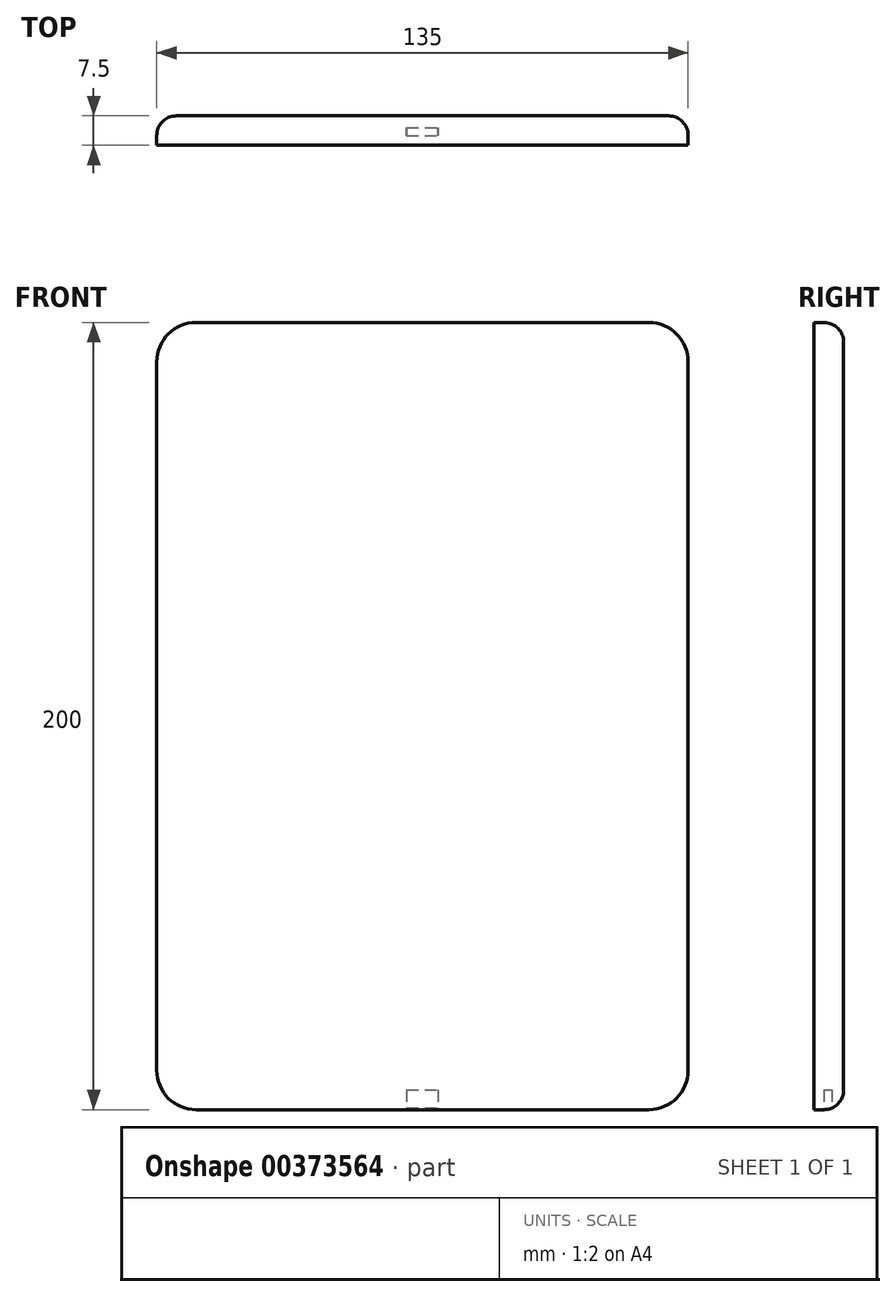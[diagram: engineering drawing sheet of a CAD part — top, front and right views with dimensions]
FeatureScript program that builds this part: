
annotation { "Feature Type Name" : "Feature", "Feature Type Description" : "" }
export const myFeature = defineFeature(function(context is Context, id is Id, definition is map)
    precondition{}
    {
        {
            var Q0;
            Q0=qCreatedBy(makeId("Front.planeOp"),FACE);
            var sketch = newSketch(context, id + "F0", { "sketchPlane" : qUnion([Q0])});
            skLineSegment(sketch, "E0.bottom", {"start": v(0, 0) * mm, "end": v(135, 0) * mm});
            skLineSegment(sketch, "E0.top", {"start": v(0, 200) * mm, "end": v(135, 200) * mm});
            skLineSegment(sketch, "E0.left", {"start": v(0, 0) * mm, "end": v(0, 200) * mm});
            skLineSegment(sketch, "E0.right", {"start": v(135, 0) * mm, "end": v(135, 200) * mm});
            skSolve(sketch);
        }
        {
            var Q0;
            Q0 = qSketchRegion(id + "F0", true);
            extrude(context, id + "F1", {"entities" : qUnion([Q0]), "depth" : 7.5 * mm});
        }
        {
            var Q0;
            Q0=makeQuery(id+"F1.opExtrude","SWEPT_EDGE",EDGE,{"disambiguationData":[OSD([sQuery(id+"F0.wireOp",EDGE,"E0.top"),sQuery(id+"F0.wireOp",EDGE,"E0.left")])]});
            var Q1;
            Q1=makeQuery(id+"F1.opExtrude","SWEPT_EDGE",EDGE,{"disambiguationData":[OSD([sQuery(id+"F0.wireOp",EDGE,"E0.top"),sQuery(id+"F0.wireOp",EDGE,"E0.right")])]});
            var Q2;
            Q2=makeQuery(id+"F1.opExtrude","SWEPT_EDGE",EDGE,{"disambiguationData":[OSD([sQuery(id+"F0.wireOp",EDGE,"E0.bottom"),sQuery(id+"F0.wireOp",EDGE,"E0.left")])]});
            var Q3;
            Q3=makeQuery(id+"F1.opExtrude","SWEPT_EDGE",EDGE,{"disambiguationData":[OSD([sQuery(id+"F0.wireOp",EDGE,"E0.bottom"),sQuery(id+"F0.wireOp",EDGE,"E0.right")])]});
            fillet(context, id + "F2", {"entities" : qUnion([Q0, Q1, Q2, Q3]), "radius" : 10 * mm, "tangentPropagation" : true, "allowEdgeOverflow" : false});
        }
        {
            var Q0;
            Q0=makeQuery(id+"F1.opExtrude","CAP_EDGE",EDGE,{"disambiguationData":[OSD([sQuery(id+"F0.wireOp",EDGE,"E0.left")])],"isStart":true});
            var Q1;
            Q1=makeQuery(id+"F1.opExtrude","CAP_EDGE",EDGE,{"disambiguationData":[OSD([sQuery(id+"F0.wireOp",EDGE,"E0.top")])],"isStart":true});
            var Q2;
            {var subQ0=sQuery(id+"F0.wireOp",EDGE,"E0.left");var subQ1=sQuery(id+"F0.wireOp",EDGE,"E0.top");Q2=makeQuery(id+"F2.opFillet","BLEND_EDGE",EDGE,{"blendedFrom":[makeQuery(id+"F1.opExtrude","SWEPT_EDGE",EDGE,{"disambiguationData":[OSD([subQ1,subQ0])]}),makeQuery(id+"F1.opExtrude","CAP_FACE",FACE,{"disambiguationData":[OSD([sQuery(id+"F0.wireOp",EDGE,"E0.bottom"),subQ1,subQ0,sQuery(id+"F0.wireOp",EDGE,"E0.right")])],"isStart":true})],"blendedInto":[makeQuery(id+"F1.opExtrude","CAP_FACE",FACE,{"disambiguationData":[OSD([sQuery(id+"F0.wireOp",EDGE,"E0.bottom"),subQ1,subQ0,sQuery(id+"F0.wireOp",EDGE,"E0.right")])],"isStart":true})]});}
            fillet(context, id + "F3", {"entities" : qUnion([Q0, Q1, Q2]), "radius" : 5 * mm, "tangentPropagation" : true, "allowEdgeOverflow" : false});
        }
        {
            var Q0;
            Q0=makeQuery(id+"F1.opExtrude","SWEPT_FACE",FACE,{"disambiguationData":[OSD([sQuery(id+"F0.wireOp",EDGE,"E0.bottom")])]});
            var sketch = newSketch(context, id + "F4", { "sketchPlane" : qUnion([Q0])});
            skLineSegment(sketch, "E1.bottom", {"start": v(63.5, 5) * mm, "end": v(71.5, 5) * mm});
            skLineSegment(sketch, "E1.top", {"start": v(63.5, 3) * mm, "end": v(71.5, 3) * mm});
            skLineSegment(sketch, "E1.left", {"start": v(63.5, 5) * mm, "end": v(63.5, 3) * mm});
            skLineSegment(sketch, "E1.right", {"start": v(71.5, 5) * mm, "end": v(71.5, 3) * mm});
            skSolve(sketch);
        }
        {
            var Q0;
            Q0 = qSketchRegion(id + "F4", true);
            extrude(context, id + "F5", {"entities" : qUnion([Q0]), "operationType" : NewBodyOperationType.REMOVE, "oppositeDirection" : true, "depth" : 5 * mm});
        }
    });
